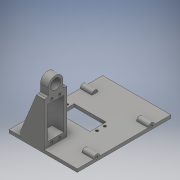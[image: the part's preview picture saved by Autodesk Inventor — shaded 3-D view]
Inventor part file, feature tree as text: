
AUTODESK INVENTOR PART (.ipt)
format: ipt  version: 2018 (Build 220112000, 112)  size: 280,064 bytes
history: native  units: mm
features: sketch x10, projected_geometry x8, extrude x7, hole x3, mirror x1
ambient origin geometry x8: Origin, YZ Plane, XZ Plane, XY Plane, X Axis, Y Axis, Z Axis, Center Point
bodies: Solid1 (feature_tree)
feature tree (29):
  extrude  "Extrusion1"  Depth=21.0mm
  hole  "Hole1"  [1 undecoded]
  extrude  "Extrusion2"  Depth=4.0mm TaperAngle=0.0deg
  hole  "Hole2"  [1 undecoded]
  mirror  "Mirror1"
  extrude  "Extrusion3"  Depth=2.0mm
  extrude  "Extrusion4"  Depth=45.0mm
  hole  "Hole3"  [1 undecoded]
  extrude  "Extrusion6"  Depth=8.0mm
  extrude  "Extrusion7"  Depth=7.0mm TaperAngle=0.0deg
  extrude  "Extrusion8"  Depth=10.0mm
  sketch  "Sketch1"  dims[d0=41.0mm d1=21.0mm]
  sketch  "Sketch2"  dims[d2=87.3mm d3=120.0mm]
  sketch  "Sketch3"  dims[d4=10.15mm d5=4.0mm d6=0.0mm]
  projected_geometry  "Projected Loop1"
  sketch  "Sketch4"  dims[d7=48.3mm d8=10.0mm]
  projected_geometry  "Projected Loop2"
  sketch  "Sketch5"  dims[d9=14.0mm]
  projected_geometry  "Projected Loop3"
  sketch  "Sketch6"  dims[d10=3.242mm d11=8.0mm d12=4.0mm d13=2.0mm d14=90.0deg d15=11.8mm d16=20.594885mm d17=70.0mm]
  projected_geometry  "Projected Loop4"
  sketch  "Sketch8"  dims[d18=15.0mm d19=0.0mm]
  projected_geometry  "Projected Loop6"
  sketch  "Sketch9"  dims[d20=3.242mm d21=8.0mm d22=4.0mm d23=2.0mm d24=90.0deg d25=11.8mm d26=20.594885mm d27=45.0mm]
  projected_geometry  "Projected Loop7"
  sketch  "Sketch10"  dims[d28=4.0mm d29=7.0mm d30=0.0mm]
  projected_geometry  "Projected Loop8"
  sketch  "Sketch11"  dims[d31=41.0mm d32=8.0mm d33=7.0mm d34=0.0mm d38=48.3mm d39=10.0mm d40=3.242mm d41=8.0mm d42=4.0mm d43=2.0mm d44=90.0deg d45=11.8mm d46=20.594885mm d47=10.0mm d48=10.0mm d49=0.0mm d50=13.0mm d51=10.0mm d52=3.0mm d53=2.0mm d54=10.0mm d55=0.0mm d56=15.0mm d57=10.0mm d58=0.0mm]
  projected_geometry  "Projected Loop9"
note: 3 required parameter values undecoded (feature->parameter linkage not recoverable at this tier; creation-order binding heuristic only, values carry confidence <= 0.55)
